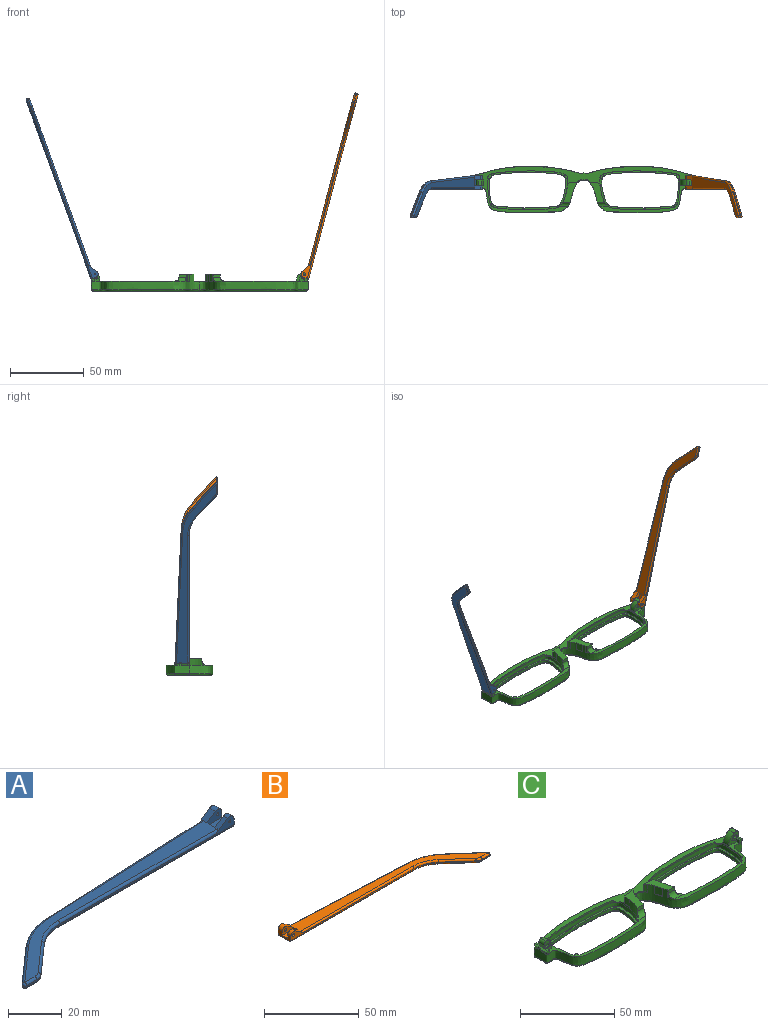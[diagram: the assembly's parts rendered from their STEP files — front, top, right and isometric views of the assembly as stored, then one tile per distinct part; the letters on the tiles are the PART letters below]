
ASSEMBLY  parts=3 mates=2
PART A: 43 faces, bbox 130.2x29.5x5.9 mm
  f0: plane 9.62x3.72mm, normal (1,0,0), area 24.7mm2, adj f1,f3,f4,f5,f10,f16,f18,f28
  f1: cylinder r=2.2mm len=3.45mm, axis (0,-1,0), area 11mm2, adj f0,f2,f4,f37
  f2: plane 6.01x3.91mm, normal (-0.55,0,0.84), area 12.7mm2, adj f1,f4,f9,f19,f37
  f3: plane 2.26x0.1mm, normal (0,0,1), area 0.1mm2, adj f0,f5,f18
  f4: plane 92.1x4.9mm, normal (0,-1,0), area 79.9mm2, adj f0,f1,f2,f14,f19,f36,f42
  f5: plane 93.42x4.13mm, normal (-0.04,1,0), area 64.8mm2, adj f0,f3,f11,f15,f17,f27,f28
  f6: plane 17.82x15.72mm, normal (-0.66,0.75,0), area 14.3mm2, adj f11,f12,f25,f30
  f7: plane 5.46x0.6mm, normal (0,-1,0), area 3.3mm2, adj f12,f13,f23,f32
  f8: plane 14.99x13.23mm, normal (0.66,-0.75,0), area 12mm2, adj f13,f14,f21,f34
  f9: plane 121.18x26.73mm, normal (0,0,1), area 627.7mm2, adj f2,f17,f19,f20,f21,f22,f23,f25
  f10: plane 129.1x27.08mm, normal (0,0,-1), area 686.5mm2, adj f0,f28,f29,f30,f32,f33,f34,f35
  f11: cylinder r=30mm len=18.52mm, axis (0,0,-1), area 12.2mm2, adj f5,f6,f26,f29
  f12: cylinder r=1mm len=1.75mm, axis (0,0,-1), area 1.5mm2, adj f6,f7,f24,f31
  f13: cylinder r=5mm len=3.31mm, axis (0,0,-1), area 2.2mm2, adj f7,f8,f22,f33
  f14: cylinder r=20mm len=13.23mm, axis (0,0,1), area 8.7mm2, adj f4,f8,f20,f35
  f15: plane 5.66x0.25mm, normal (0,0,-1), area 0.7mm2, adj f5,f17,f18
  f16: cylinder r=2.2mm len=3.45mm, axis (0,-1,0), area 14.8mm2, adj f0,f17,f18,f38
  f17: plane 6.01x3.91mm, normal (-0.55,0,0.84), area 16.9mm2, adj f5,f9,f15,f16,f18,f27,f38
  f18: plane 7.92x3.3mm, normal (0,1,0), area 15.9mm2, adj f0,f3,f15,f16,f17,f41
  f19: cylinder r=1mm len=84.18mm, axis (-1,0,0), area 131.4mm2, adj f2,f4,f9,f20
  f20: torus R=21mm, axis (0,0,1), area 23.1mm2, adj f9,f14,f19,f21
  f21: cylinder r=1mm len=15.65mm, axis (-0.75,-0.66,0), area 31.4mm2, adj f8,f9,f20,f22
  f22: torus R=4mm, axis (0,0,1), area 5.3mm2, adj f9,f13,f21,f23
  f23: cylinder r=1mm len=5.46mm, axis (-1,0,0), area 8.6mm2, adj f7,f9,f22,f24
  f24: sphere r=1mm, area 2.4mm2, adj f12,f23,f25
  f25: cylinder r=1mm len=18.48mm, axis (0.75,0.66,0), area 37.3mm2, adj f6,f9,f24,f26
  f26: torus R=29mm, axis (0,0,1), area 31.6mm2, adj f9,f11,f25,f27
  f27: cylinder r=1mm len=85.5mm, axis (1,0.04,0), area 133.5mm2, adj f5,f9,f17,f26
  f28: cylinder r=1mm len=93.46mm, axis (-1,-0.04,0), area 146.9mm2, adj f0,f5,f10,f29
  f29: torus R=29mm, axis (0,0,1), area 31.6mm2, adj f10,f11,f28,f30
  f30: cylinder r=1mm len=18.48mm, axis (-0.75,-0.66,0), area 37.3mm2, adj f6,f10,f29,f31
  f31: sphere r=1mm, area 2.4mm2, adj f12,f30,f32
  f32: cylinder r=1mm len=5.46mm, axis (1,0,0), area 8.6mm2, adj f7,f10,f31,f33
  f33: torus R=4mm, axis (0,0,1), area 5.3mm2, adj f10,f13,f32,f34
  f34: cylinder r=1mm len=15.65mm, axis (0.75,0.66,0), area 31.4mm2, adj f8,f10,f33,f35
  f35: torus R=21mm, axis (0,0,1), area 23.1mm2, adj f10,f14,f34,f36
  f36: cylinder r=1mm len=92.1mm, axis (1,0,0), area 144.7mm2, adj f0,f4,f10,f35
  f37: plane 7.92x4.7mm, normal (0,1,0), area 27mm2, adj f0,f1,f2,f39,f40,f42
  f38: plane 7.92x4.7mm, normal (0,-1,0), area 27mm2, adj f0,f16,f17,f39,f40,f41
  f39: plane 7.92x4.1mm, normal (0,0,1), area 32.5mm2, adj f0,f37,f38,f40
  f40: plane 4.1x1.4mm, normal (1,0,0), area 5.7mm2, adj f9,f37,f38,f39
  f41: cylinder r=0.5mm len=3.1mm, axis (0,-1,0), area 9.7mm2, adj f18,f38
  f42: cylinder r=0.5mm len=2.3mm, axis (0,-1,0), area 7.2mm2, adj f4,f37
PART B: 43 faces, bbox 130.2x29.5x5.9 mm
  f0: plane 9.62x3.72mm, normal (-1,0,0), area 24.7mm2, adj f1,f3,f4,f5,f10,f16,f18,f28
  f1: cylinder r=2.2mm len=3.45mm, axis (0,-1,0), area 11mm2, adj f0,f2,f4,f37
  f2: plane 6.01x3.91mm, normal (0.55,0,0.84), area 12.7mm2, adj f1,f4,f9,f19,f37
  f3: plane 2.26x0.1mm, normal (0,0,1), area 0.1mm2, adj f0,f5,f18
  f4: plane 92.1x4.9mm, normal (0,-1,0), area 78.2mm2, adj f0,f1,f2,f14,f19,f36,f42
  f5: plane 93.42x4.13mm, normal (0.04,1,0), area 64.8mm2, adj f0,f3,f11,f15,f17,f27,f28
  f6: plane 17.82x15.72mm, normal (0.66,0.75,0), area 14.3mm2, adj f11,f12,f25,f30
  f7: plane 5.46x0.6mm, normal (0,-1,0), area 3.3mm2, adj f12,f13,f23,f32
  f8: plane 14.99x13.23mm, normal (-0.66,-0.75,0), area 12mm2, adj f13,f14,f21,f34
  f9: plane 121.18x26.73mm, normal (0,0,1), area 627.7mm2, adj f2,f17,f19,f20,f21,f22,f23,f25
  f10: plane 129.1x27.08mm, normal (0,0,-1), area 686.5mm2, adj f0,f28,f29,f30,f32,f33,f34,f35
  f11: cylinder r=30mm len=18.52mm, axis (0,0,-1), area 12.2mm2, adj f5,f6,f26,f29
  f12: cylinder r=1mm len=1.75mm, axis (0,0,-1), area 1.5mm2, adj f6,f7,f24,f31
  f13: cylinder r=5mm len=3.31mm, axis (0,0,-1), area 2.2mm2, adj f7,f8,f22,f33
  f14: cylinder r=20mm len=13.23mm, axis (0,0,1), area 8.7mm2, adj f4,f8,f20,f35
  f15: plane 5.66x0.25mm, normal (0,0,-1), area 0.7mm2, adj f5,f17,f18
  f16: cylinder r=2.2mm len=3.45mm, axis (0,-1,0), area 14.8mm2, adj f0,f17,f18,f38
  f17: plane 6.01x3.91mm, normal (0.55,0,0.84), area 16.9mm2, adj f5,f9,f15,f16,f18,f27,f38
  f18: plane 7.92x3.3mm, normal (0,1,0), area 14.3mm2, adj f0,f3,f15,f16,f17,f41
  f19: cylinder r=1mm len=84.18mm, axis (1,0,0), area 131.4mm2, adj f2,f4,f9,f20
  f20: torus R=21mm, axis (0,0,1), area 23.1mm2, adj f9,f14,f19,f21
  f21: cylinder r=1mm len=15.65mm, axis (0.75,-0.66,0), area 31.4mm2, adj f8,f9,f20,f22
  f22: torus R=4mm, axis (0,0,1), area 5.3mm2, adj f9,f13,f21,f23
  f23: cylinder r=1mm len=5.46mm, axis (1,0,0), area 8.6mm2, adj f7,f9,f22,f24
  f24: sphere r=1mm, area 2.4mm2, adj f12,f23,f25
  f25: cylinder r=1mm len=18.48mm, axis (-0.75,0.66,0), area 37.3mm2, adj f6,f9,f24,f26
  f26: torus R=29mm, axis (0,0,1), area 31.6mm2, adj f9,f11,f25,f27
  f27: cylinder r=1mm len=85.5mm, axis (-1,0.04,0), area 133.5mm2, adj f5,f9,f17,f26
  f28: cylinder r=1mm len=93.46mm, axis (1,-0.04,0), area 146.9mm2, adj f0,f5,f10,f29
  f29: torus R=29mm, axis (0,0,1), area 31.6mm2, adj f10,f11,f28,f30
  f30: cylinder r=1mm len=18.48mm, axis (0.75,-0.66,0), area 37.3mm2, adj f6,f10,f29,f31
  f31: sphere r=1mm, area 2.4mm2, adj f12,f30,f32
  f32: cylinder r=1mm len=5.46mm, axis (-1,0,0), area 8.6mm2, adj f7,f10,f31,f33
  f33: torus R=4mm, axis (0,0,1), area 5.3mm2, adj f10,f13,f32,f34
  f34: cylinder r=1mm len=15.65mm, axis (-0.75,0.66,0), area 31.4mm2, adj f8,f10,f33,f35
  f35: torus R=21mm, axis (0,0,1), area 23.1mm2, adj f10,f14,f34,f36
  f36: cylinder r=1mm len=92.1mm, axis (-1,0,0), area 144.7mm2, adj f0,f4,f10,f35
  f37: plane 7.92x4.7mm, normal (0,1,0), area 25.4mm2, adj f0,f1,f2,f39,f40,f42
  f38: plane 7.92x4.7mm, normal (0,-1,0), area 25.4mm2, adj f0,f16,f17,f39,f40,f41
  f39: plane 7.92x4.1mm, normal (0,0,1), area 32.5mm2, adj f0,f37,f38,f40
  f40: plane 4.1x1.4mm, normal (-1,0,0), area 5.7mm2, adj f9,f37,f38,f39
  f41: cylinder r=0.88mm len=3.1mm, axis (0,-1,0), area 17mm2, adj f18,f38
  f42: cylinder r=0.88mm len=2.3mm, axis (0,-1,0), area 12.6mm2, adj f4,f37
PART C: 134 faces, bbox 148x33.2x13.8 mm
  f0: plane 6.36x4.1mm, normal (0,-1,0), area 11.1mm2, adj f1,f128,f129,f130,f131,f132,f133
  f1: plane 3.31x1.2mm, normal (-0.94,0,0.34), area 0.1mm2, adj f0,f2,f128,f133
  f2: plane 5.76x5.02mm, normal (0,-1,0), area 14.3mm2, adj f1,f3,f123,f124,f125,f126,f127,f133
  f3: plane 4x2.21mm, normal (0.94,0,-0.34), area 9.4mm2, adj f2,f4,f123,f126
  f4: plane 6.96x5.07mm, normal (0,1,0), area 20mm2, adj f3,f5,f122,f123,f126,f127,f130,f133
  f5: plane 3.39x2.1mm, normal (-1,0,0), area 7.1mm2, adj f4,f6,f123,f130
  f6: plane 2.1x1.72mm, normal (0,1,0), area 2.9mm2, adj f5,f7,f121,f123,f130
  f7: cylinder r=1mm len=2.28mm, axis (-0.34,0,-0.94), area 3mm2, adj f6,f8,f121,f130
  f8: plane 1.96x1.6mm, normal (0.94,0,-0.34), area 3.3mm2, adj f7,f9,f121,f130
  f9: cone r=1mm half-angle=20deg, axis (0,0,1), area 0mm2, adj f8,f10,f120,f130
  f10: plane 1.81x0.58mm, normal (-0.02,-1,0), area 0.5mm2, adj f9,f11,f120
  f11: extruded ~73.56x31.7mm, area 719mm2, adj f10,f12,f13,f14,f15,f16,f68,f69
  f12: plane 2.01x1.35mm, normal (0,0,1), area 0mm2, adj f11,f13
  f13: extruded ~5x1.98mm, area 11.9mm2, adj f11,f12,f16,f119
  f14: bspline ~6.2x2.02mm, area 0mm2, adj f11,f15
  f15: extruded ~5.3x4.93mm, area 27.2mm2, adj f11,f14,f16
  f16: plane 13.49x10.15mm, normal (0,0,1), area 63mm2, adj f11,f13,f15,f17,f19,f67,f69,f119
  f17: extruded ~5x4.08mm, area 20.6mm2, adj f16,f18,f19,f119
  f18: plane 4.12x0.61mm, normal (0,0,1), area 0.4mm2, adj f17,f19
  f19: extruded ~54.37x26.52mm, area 194.2mm2, adj f16,f17,f18,f20,f21,f22,f61,f62
  f20: plane 3.49x2.64mm, normal (0,0,-1), area 5.9mm2, adj f19,f21
  f21: cylinder r=2.28mm len=3.42mm, axis (0,0,1), area 2.6mm2, adj f19,f20,f130
  f22: extruded ~54.37x26.52mm, area 385.2mm2, adj f19,f23
  f23: plane 54.58x26.63mm, normal (0,0,1), area 165.6mm2, adj f22,f24
  f24: extruded ~51.72x24.32mm, area 239.3mm2, adj f23,f25
  f25: bspline ~54.07x26.32mm, area 218.4mm2, adj f24,f26
  f26: plane 144.85x29.71mm, normal (0,0,-1), area 720.9mm2, adj f25,f27,f53,f54,f56,f58,f60,f82
  f27: bspline ~54.07x26.32mm, area 218.4mm2, adj f26,f28
  f28: extruded ~51.72x24.32mm, area 239.3mm2, adj f27,f29
  f29: plane 54.58x26.63mm, normal (0,0,1), area 165.6mm2, adj f28,f30
  f30: extruded ~54.37x26.52mm, area 385.2mm2, adj f29,f31
  f31: extruded ~54.37x26.52mm, area 194.2mm2, adj f30,f32,f33,f34,f35,f36,f37,f42
  f32: plane 3.49x2.64mm, normal (0,0,-1), area 5.9mm2, adj f31,f33
  f33: cylinder r=2.28mm len=3.42mm, axis (0,0,1), area 2.6mm2, adj f31,f32,f130
  f34: plane 3.28x2.39mm, normal (0,0,-1), area 4.5mm2, adj f31,f35
  f35: cylinder r=2.28mm len=3.22mm, axis (0,0,1), area 2.3mm2, adj f31,f34,f130
  f36: plane 4.12x0.61mm, normal (0,0,1), area 0.4mm2, adj f31,f37
  f37: extruded ~5x4.08mm, area 20.6mm2, adj f31,f36,f38,f42
  f38: plane 7.09x5.4mm, normal (-0.09,1,0), area 35.1mm2, adj f37,f39,f40,f42,f87,f130
  f39: bspline ~5.24x2.55mm, area 2.2mm2, adj f38,f87,f118,f130
  f40: extruded ~5x1.98mm, area 11.9mm2, adj f38,f41,f42,f87
  f41: plane 2.01x1.35mm, normal (0,0,1), area 0mm2, adj f40,f87
  f42: plane 13.49x10.15mm, normal (0,0,1), area 63mm2, adj f31,f37,f38,f40,f43,f45,f47,f87
  f43: extruded ~5.3x4.93mm, area 27.2mm2, adj f42,f44,f87
  f44: bspline ~7.04x2.22mm, area 0mm2, adj f43,f87
  f45: extruded ~5x0.83mm, area 4.3mm2, adj f42,f46,f47,f87
  f46: plane 0.83x0.25mm, normal (0,0,1), area 0mm2, adj f45,f87
  f47: plane 4.84x2mm, normal (0,-1,0), area 9.7mm2, adj f31,f42,f45,f48
  f48: cylinder r=3mm len=7.65mm, axis (-1,0,0), area 24.4mm2, adj f31,f47,f50,f87,f130
  f49: plane 2.01x1.94mm, normal (0,0,-1), area 2.1mm2, adj f31,f50
  f50: cylinder r=1.3mm len=1.99mm, axis (0,0,1), area 2.5mm2, adj f31,f48,f49,f130
  f51: plane 2.16x2.07mm, normal (0,0,-1), area 2.5mm2, adj f31,f52
  f52: cylinder r=1.3mm len=2.11mm, axis (0,0,1), area 1.8mm2, adj f31,f51,f130
  f53: bspline ~43.39x5.71mm, area 65.2mm2, adj f26,f54,f81,f82
  f54: bspline ~43.39x5.71mm, area 65.2mm2, adj f26,f53,f55,f56
  f55: extruded ~41.05x5.5mm, area 228.4mm2, adj f54,f81,f87,f130
  f56: bspline ~49.4x7.94mm, area 50.9mm2, adj f26,f54,f57,f87
  f57: bspline ~1.15x1mm, area 0.7mm2, adj f56,f58,f87
  f58: bspline ~9.22x1.42mm, area 12.7mm2, adj f26,f57,f59,f87
  f59: bspline ~1x1mm, area 0.8mm2, adj f58,f60,f87
  f60: bspline ~73.15x23.36mm, area 150.1mm2, adj f26,f59,f86,f87
  f61: plane 3.28x2.39mm, normal (0,0,-1), area 4.5mm2, adj f19,f62
  f62: cylinder r=2.28mm len=3.22mm, axis (0,0,1), area 2.3mm2, adj f19,f61,f130
  f63: plane 2.01x1.94mm, normal (0,0,-1), area 2.1mm2, adj f19,f64
  f64: cylinder r=1.3mm len=1.99mm, axis (0,0,1), area 2.5mm2, adj f19,f63,f70,f130
  f65: cylinder r=1.3mm len=2.11mm, axis (0,0,1), area 1.8mm2, adj f19,f66,f130
  f66: plane 2.16x2.07mm, normal (0,0,-1), area 2.5mm2, adj f19,f65
  f67: plane 4.84x2mm, normal (0,-1,0), area 9.7mm2, adj f16,f19,f69,f70
  f68: plane 0.83x0.25mm, normal (0,0,1), area 0mm2, adj f11,f69
  f69: extruded ~5x0.83mm, area 4.3mm2, adj f11,f16,f67,f68
  f70: cylinder r=3mm len=7.65mm, axis (1,0,0), area 24.4mm2, adj f11,f19,f64,f67,f130
  f71: plane 1.41x0.07mm, normal (0,0,1), area 0.1mm2, adj f11,f72,f78
  f72: plane 2.69x2.41mm, normal (0,-1,0), area 4.1mm2, adj f71,f73,f77,f123,f124
  f73: plane 5.02x1.43mm, normal (0.34,0,0.94), area 7.2mm2, adj f72,f74,f76,f77,f123
  f74: cone r=1mm half-angle=70deg, axis (0,0,-1), area 0mm2, adj f73,f75,f79,f80
  f75: cone r=1mm half-angle=20deg, axis (0,0,1), area 0mm2, adj f74,f76,f78,f79
  f76: plane 4.02x1.6mm, normal (0.94,0,-0.34), area 6.8mm2, adj f73,f75,f77,f78
  f77: cone r=1mm half-angle=20deg, axis (0,0,1), area 2.1mm2, adj f72,f73,f76,f78
  f78: plane 5.16x1.21mm, normal (0,0,1), area 0.4mm2, adj f11,f71,f75,f76,f77
  f79: plane 1.81x0.58mm, normal (-0.01,1,0), area 0.5mm2, adj f11,f74,f75
  f80: bspline ~1.76x1.05mm, area 1.5mm2, adj f11,f74,f120,f123
  f81: extruded ~41.05x5.5mm, area 228.4mm2, adj f11,f53,f55,f130
  f82: bspline ~36.63x7.13mm, area 50.8mm2, adj f11,f26,f53,f83
  f83: bspline ~1.15x1mm, area 0.7mm2, adj f11,f82,f84
  f84: bspline ~9.22x1.42mm, area 12.7mm2, adj f11,f26,f83,f85
  f85: bspline ~1x1mm, area 0.8mm2, adj f11,f84,f86
  f86: bspline ~73.15x23.36mm, area 150.1mm2, adj f11,f26,f60,f85
  f87: extruded ~73.56x31.7mm, area 719mm2, adj f11,f38,f39,f40,f41,f42,f43,f44
  f88: plane 1.41x0.07mm, normal (0,0,1), area 0.1mm2, adj f87,f89,f114
  f89: plane 2.69x2.41mm, normal (0,-1,0), area 4.1mm2, adj f88,f90,f94,f112,f113
  f90: plane 5.02x1.43mm, normal (-0.34,0,0.94), area 7.2mm2, adj f89,f91,f93,f94,f113
  f91: plane 4.02x1.6mm, normal (-0.94,0,-0.34), area 6.8mm2, adj f90,f92,f113,f114
  f92: cone r=1mm half-angle=20deg, axis (0,0,1), area 0mm2, adj f91,f93,f114,f115
  f93: cone r=1mm half-angle=70deg, axis (0,0,-1), area 0mm2, adj f90,f92,f115,f116
  f94: plane 9.81x1.4mm, normal (0,0,1), area 8.6mm2, adj f89,f90,f95,f100,f101,f102,f110,f111
  f95: plane 2.96x1.38mm, normal (-0.34,0,0.94), area 4.1mm2, adj f94,f96,f98,f99,f100
  f96: cone r=1mm half-angle=70deg, axis (0,0,-1), area 0mm2, adj f95,f97,f116,f117
  f97: cone r=1mm half-angle=20deg, axis (0,0,1), area 0mm2, adj f96,f98,f117,f130
  f98: plane 1.96x1.6mm, normal (-0.94,0,-0.34), area 3.3mm2, adj f95,f97,f99,f130
  f99: cylinder r=1mm len=2.28mm, axis (0.34,0,-0.94), area 3mm2, adj f95,f98,f100,f130
  f100: plane 2.1x1.72mm, normal (0,1,0), area 2.9mm2, adj f94,f95,f99,f101,f130
  f101: plane 3.39x2.1mm, normal (1,0,0), area 7.1mm2, adj f94,f100,f102,f130
  f102: plane 6.96x5.07mm, normal (0,1,0), area 20mm2, adj f94,f101,f103,f104,f105,f107,f108,f109
  f103: cylinder r=1.98mm len=4mm, axis (0,1,0), area 12.4mm2, adj f102,f104,f108,f111
  f104: cylinder r=1.98mm len=4mm, axis (0,-1,0), area 12.4mm2, adj f102,f103,f110,f111
  f105: plane 4x2.36mm, normal (1,0,0), area 9.5mm2, adj f102,f106,f107,f130
  f106: plane 3.21x2.36mm, normal (0,-1,0), area 5.7mm2, adj f105,f107,f111,f112,f130
  f107: plane 4x0.05mm, normal (-0.34,0,0.94), area 0.2mm2, adj f102,f105,f106,f108
  f108: plane 4x3.31mm, normal (0.94,0,0.34), area 14.1mm2, adj f102,f103,f107,f111
  f109: cylinder r=1.25mm len=4mm, axis (0,-1,0), area 31.4mm2, adj f102,f111
  f110: plane 4x2.21mm, normal (-0.94,0,-0.34), area 9.4mm2, adj f94,f102,f104,f111
  f111: plane 5.76x5.02mm, normal (0,-1,0), area 14.3mm2, adj f94,f103,f104,f106,f108,f109,f110,f112
  f112: plane 2.29x2.1mm, normal (1,0,0), area 4.8mm2, adj f89,f94,f106,f111,f130
  f113: cone r=1mm half-angle=20deg, axis (0,0,1), area 2.1mm2, adj f89,f90,f91,f114
  f114: plane 5.16x1.21mm, normal (0,0,1), area 0.4mm2, adj f87,f88,f91,f92,f113
  f115: plane 1.81x0.58mm, normal (0.01,1,0), area 0.5mm2, adj f87,f92,f93
  f116: bspline ~1.76x1.05mm, area 1.5mm2, adj f87,f93,f94,f96
  f117: plane 1.81x0.58mm, normal (0.02,-1,0), area 0.5mm2, adj f87,f96,f97
  f118: bspline ~5.24x2.55mm, area 2.2mm2, adj f11,f39,f119,f130
  f119: plane 7.09x5.4mm, normal (0.09,1,0), area 35.1mm2, adj f11,f13,f16,f17,f118,f130
  f120: cone r=1mm half-angle=70deg, axis (0,0,-1), area 0mm2, adj f9,f10,f80,f121
  f121: plane 2.96x1.38mm, normal (0.34,0,0.94), area 4.1mm2, adj f6,f7,f8,f120,f123
  f122: plane 6.36x4.1mm, normal (0,1,0), area 11.1mm2, adj f4,f130,f131,f132
  f123: plane 9.81x1.4mm, normal (0,0,1), area 8.6mm2, adj f2,f3,f4,f5,f6,f72,f73,f80
  f124: plane 2.29x2.1mm, normal (-1,0,0), area 4.8mm2, adj f2,f72,f123,f125,f130
  f125: plane 3.21x2.36mm, normal (0,-1,0), area 5.7mm2, adj f2,f124,f128,f129,f130
  f126: cylinder r=1.98mm len=4mm, axis (0,-1,0), area 12.4mm2, adj f2,f3,f4,f133
  f127: cylinder r=1.25mm len=4mm, axis (0,-1,0), area 31.4mm2, adj f2,f4
  f128: plane 0.05x0.02mm, normal (0.34,0,0.94), area 0mm2, adj f0,f1,f125,f129
  f129: plane 2.36x0.01mm, normal (-1,0,0), area 0mm2, adj f0,f125,f128,f130
  f130: plane 147.69x31.91mm, normal (0,0,1), area 842.2mm2, adj f0,f4,f5,f6,f7,f8,f9,f11
  f131: plane 3.99x0.02mm, normal (-1,0,0), area 0.1mm2, adj f0,f122,f130,f132
  f132: cylinder r=6.96mm len=6.35mm, axis (0,-1,0), area 31.8mm2, adj f0,f122,f131,f133
  f133: cylinder r=1.98mm len=4mm, axis (0,1,0), area 9mm2, adj f0,f1,f2,f4,f126,f132
PLACE A rot(axis=(0,1,0),70deg) t=(-84.8,-5.75,55.99)mm
PLACE B rot(axis=(0,-1,0),75deg) t=(68.2,-5.75,-61.61)mm
PLACE C t=(10.15,-1.13,-7.52)mm
MATE revolute A.f1 <-> C.f103  axis (0,-1,0) through (-60.92,2.72,1.21)mm
MATE revolute B.f41 <-> C.f126  axis (0,-1,0) through (81.2,2.72,1.21)mm
